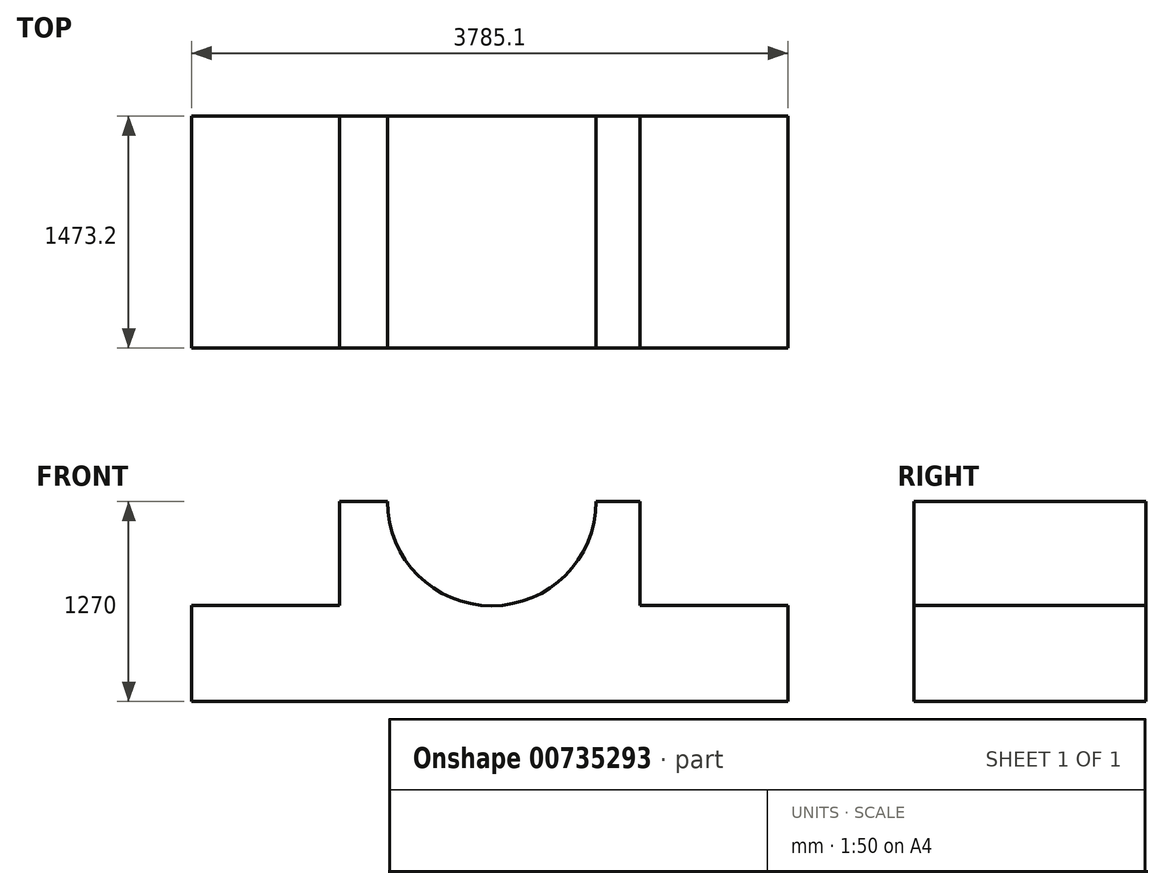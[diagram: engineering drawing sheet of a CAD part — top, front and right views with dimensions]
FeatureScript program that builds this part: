
annotation { "Feature Type Name" : "Feature", "Feature Type Description" : "" }
export const myFeature = defineFeature(function(context is Context, id is Id, definition is map)
    precondition{}
    {
        {
            var Q0;
            Q0=qCreatedBy(makeId("Front.planeOp"),FACE);
            var sketch = newSketch(context, id + "F0", { "sketchPlane" : qUnion([Q0])});
            skLineSegment(sketch, "E0", {"start": v(-24.9, 0) * mm, "end": v(3785.1, 0) * mm});
            skLineSegment(sketch, "E1", {"start": v(0, 0) * mm, "end": v(0, 609.6) * mm});
            skLineSegment(sketch, "E2", {"start": v(0, 609.6) * mm, "end": v(939.8, 609.6) * mm});
            skLineSegment(sketch, "E3", {"start": v(939.8, 609.6) * mm, "end": v(939.8, 1270) * mm});
            skLineSegment(sketch, "E4", {"start": v(939.8, 1270) * mm, "end": v(1244.6, 1270) * mm});
            skLineSegment(sketch, "E5", {"start": v(1244.6, 1270) * mm, "end": v(1905, 1270) * mm});
            skLineSegment(sketch, "E6", {"start": v(3785.1, 0) * mm, "end": v(3785.1, 609.6) * mm});
            skLineSegment(sketch, "E7", {"start": v(3785.1, 609.6) * mm, "end": v(2845.3, 609.6) * mm});
            skLineSegment(sketch, "E8", {"start": v(2845.3, 609.6) * mm, "end": v(2845.3, 1270) * mm});
            skLineSegment(sketch, "E9", {"start": v(2845.3, 1270) * mm, "end": v(2540.5, 1270) * mm});
            skCircle(sketch, "E10", {"center": v(1905, 1270) * mm, "radius": 662.58 * mm});
            skSolve(sketch);
        }
        {
            var Q0;
            {var subQ1=sQuery(id+"F0.wireOp",EDGE,"E1");Q0=makeQuery(id+"F0.imprint","IMPRINT",FACE,{"disambiguationData":[TD([[makeQuery(id+"F0.imprint","IMPRINT",EDGE,{"derivedFrom":subQ1}),-1.0]])]});}
            extrude(context, id + "F1", {"entities" : qUnion([Q0]), "depth" : 1473.2 * mm, "offsetDistance" : 25.4 * mm});
        }
    });
